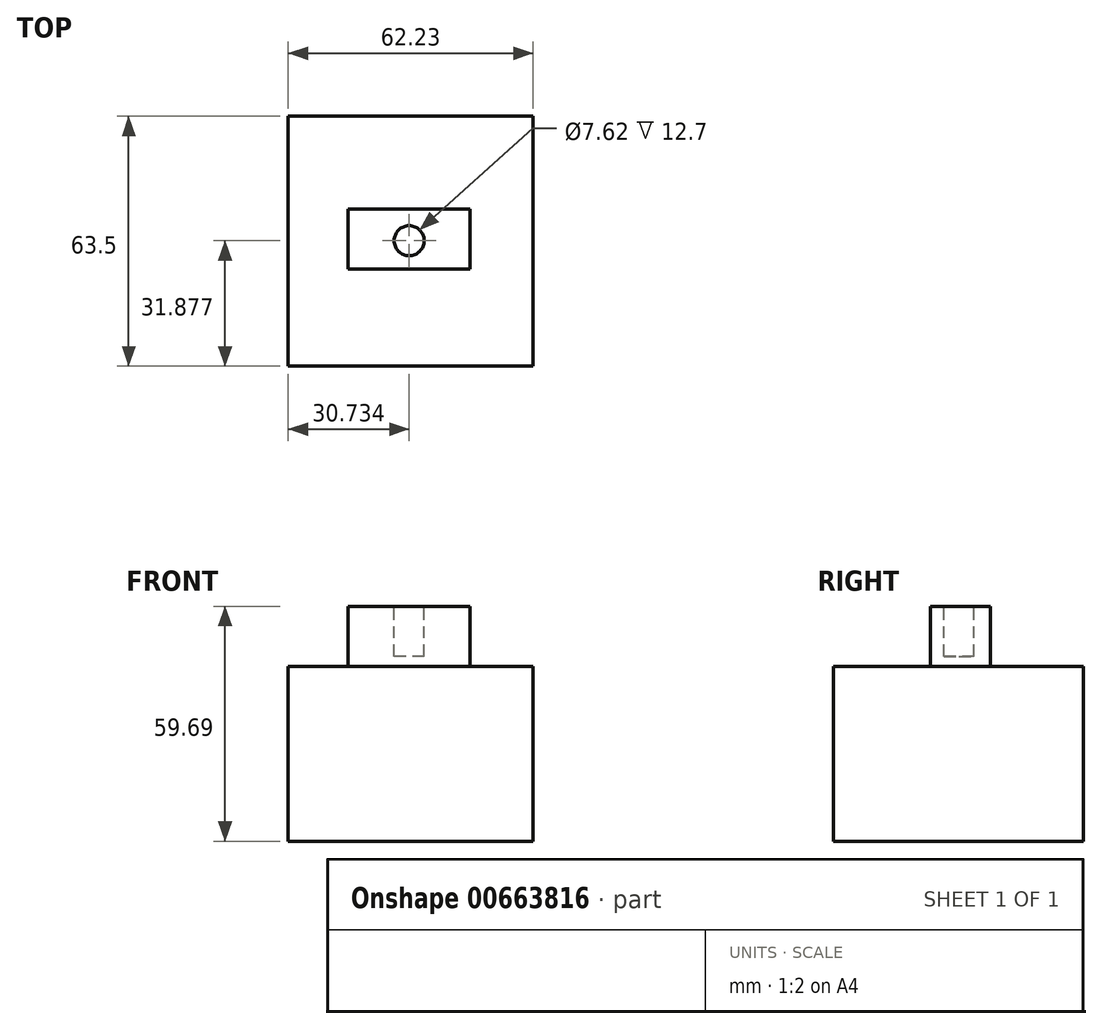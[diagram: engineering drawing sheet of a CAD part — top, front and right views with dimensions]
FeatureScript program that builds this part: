
annotation { "Feature Type Name" : "Feature", "Feature Type Description" : "" }
export const myFeature = defineFeature(function(context is Context, id is Id, definition is map)
    precondition{}
    {
        {
            var Q0;
            Q0=qCreatedBy(makeId("Top.planeOp"),FACE);
            var sketch = newSketch(context, id + "F0", { "sketchPlane" : qUnion([Q0])});
            skLineSegment(sketch, "E0.bottom", {"start": v(0, 0) * mm, "end": v(62.23, 0) * mm});
            skLineSegment(sketch, "E0.top", {"start": v(0, 63.5) * mm, "end": v(62.23, 63.5) * mm});
            skLineSegment(sketch, "E0.left", {"start": v(0, 0) * mm, "end": v(0, 63.5) * mm});
            skLineSegment(sketch, "E0.right", {"start": v(62.23, 0) * mm, "end": v(62.23, 63.5) * mm});
            skSolve(sketch);
        }
        {
            var Q0;
            Q0 = qSketchRegion(id + "F0", true);
            extrude(context, id + "F1", {"entities" : qUnion([Q0]), "oppositeDirection" : true, "depth" : 44.45 * mm, "offsetDistance" : 25.4 * mm});
        }
        {
            var Q0;
            Q0=makeQuery(id+"F1.opExtrude","CAP_FACE",FACE,{"disambiguationData":[OSD([sQuery(id+"F0.wireOp",EDGE,"E0.bottom"),sQuery(id+"F0.wireOp",EDGE,"E0.top"),sQuery(id+"F0.wireOp",EDGE,"E0.left"),sQuery(id+"F0.wireOp",EDGE,"E0.right")])],"isStart":true});
            var sketch = newSketch(context, id + "F2", { "sketchPlane" : qUnion([Q0])});
            skLineSegment(sketch, "E1.bottom", {"start": v(15.24, 39.88) * mm, "end": v(46.23, 39.88) * mm});
            skLineSegment(sketch, "E1.top", {"start": v(15.24, 24.64) * mm, "end": v(46.23, 24.64) * mm});
            skLineSegment(sketch, "E1.left", {"start": v(15.24, 39.88) * mm, "end": v(15.24, 24.64) * mm});
            skLineSegment(sketch, "E1.right", {"start": v(46.23, 39.88) * mm, "end": v(46.23, 24.64) * mm});
            skSolve(sketch);
        }
        {
            var Q0;
            Q0 = qSketchRegion(id + "F2", true);
            extrude(context, id + "F3", {"entities" : qUnion([Q0]), "operationType" : NewBodyOperationType.ADD, "depth" : 15.24 * mm, "offsetDistance" : 25.4 * mm});
        }
        {
            var Q0;
            Q0=makeQuery(id+"F3.opExtrude","CAP_FACE",FACE,{"disambiguationData":[OSD([sQuery(id+"F2.wireOp",EDGE,"E1.bottom"),sQuery(id+"F2.wireOp",EDGE,"E1.top"),sQuery(id+"F2.wireOp",EDGE,"E1.left"),sQuery(id+"F2.wireOp",EDGE,"E1.right")])],"isStart":false});
            var sketch = newSketch(context, id + "F4", { "sketchPlane" : qUnion([Q0])});
            skCircle(sketch, "E2", {"center": v(30.73, 31.88) * mm, "radius": 3.81 * mm});
            skSolve(sketch);
        }
        {
            var Q0;
            Q0=makeQuery(id+"F4.imprint","IMPRINT",FACE,{"disambiguationData":[TD([[makeQuery(id+"F4.imprint","IMPRINT",EDGE,{"derivedFrom":sQuery(id+"F4.wireOp",EDGE,"E2")}),1.0]])]});
            extrude(context, id + "F5", {"entities" : qUnion([Q0]), "operationType" : NewBodyOperationType.REMOVE, "oppositeDirection" : true, "depth" : 12.7 * mm, "offsetDistance" : 25.4 * mm});
        }
    });
